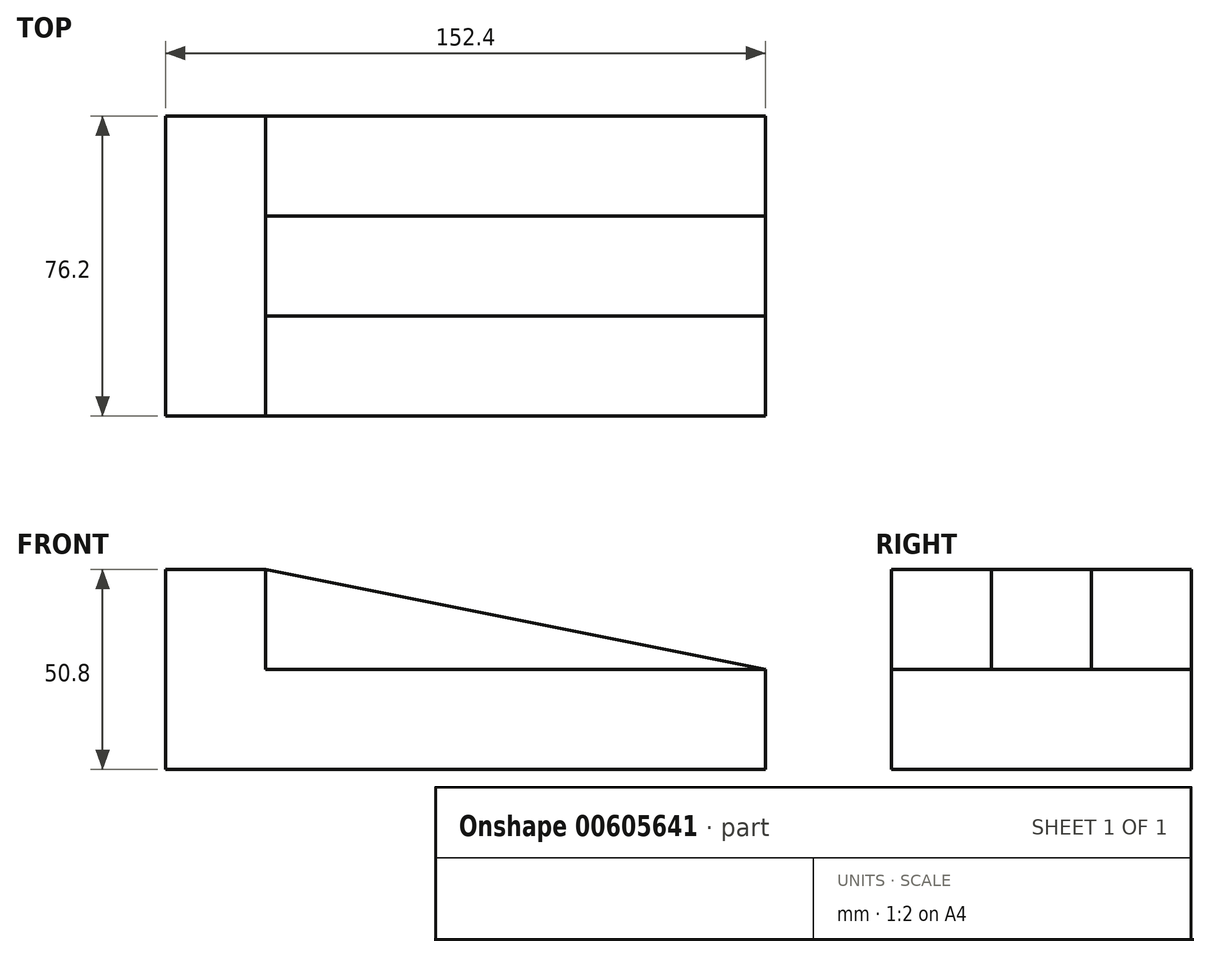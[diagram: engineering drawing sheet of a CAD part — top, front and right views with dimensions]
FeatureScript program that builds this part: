
annotation { "Feature Type Name" : "Feature", "Feature Type Description" : "" }
export const myFeature = defineFeature(function(context is Context, id is Id, definition is map)
    precondition{}
    {
        {
            var Q0;
            Q0=qCreatedBy(makeId("Front.planeOp"),FACE);
            var sketch = newSketch(context, id + "F0", { "sketchPlane" : qUnion([Q0])});
            skLineSegment(sketch, "E0", {"start": v(0, 0) * mm, "end": v(152.4, 0) * mm});
            skLineSegment(sketch, "E1", {"start": v(152.4, 0) * mm, "end": v(152.4, 50.8) * mm});
            skLineSegment(sketch, "E2", {"start": v(152.4, 50.8) * mm, "end": v(0, 50.8) * mm});
            skLineSegment(sketch, "E3", {"start": v(0, 50.8) * mm, "end": v(0, 0) * mm});
            skSolve(sketch);
        }
        {
            var Q0;
            Q0 = qSketchRegion(id + "F0", true);
            extrude(context, id + "F1", {"entities" : qUnion([Q0]), "depth" : 76.2 * mm, "offsetDistance" : 25.4 * mm});
        }
        {
            var Q0;
            Q0=makeQuery(id+"F1.opExtrude","CAP_FACE",FACE,{"disambiguationData":[OSD([sQuery(id+"F0.wireOp",EDGE,"E0"),sQuery(id+"F0.wireOp",EDGE,"E1"),sQuery(id+"F0.wireOp",EDGE,"E2"),sQuery(id+"F0.wireOp",EDGE,"E3")])],"isStart":false});
            var sketch = newSketch(context, id + "F2", { "sketchPlane" : qUnion([Q0])});
            skLineSegment(sketch, "E4", {"start": v(0, 50.8) * mm, "end": v(25.4, 50.8) * mm});
            skLineSegment(sketch, "E5", {"start": v(25.4, 50.8) * mm, "end": v(25.4, 25.4) * mm});
            skLineSegment(sketch, "E6", {"start": v(25.4, 25.4) * mm, "end": v(152.4, 25.4) * mm});
            skLineSegment(sketch, "E7", {"start": v(0, 50.8) * mm, "end": v(0, 0) * mm});
            skLineSegment(sketch, "E8", {"start": v(0, 0) * mm, "end": v(152.4, 0) * mm});
            skLineSegment(sketch, "E9", {"start": v(152.4, 0) * mm, "end": v(152.4, 25.4) * mm});
            skLineSegment(sketch, "E10", {"start": v(152.4, 25.4) * mm, "end": v(152.4, 0) * mm});
            skLineSegment(sketch, "E11", {"start": v(152.4, 0) * mm, "end": v(0, 0) * mm});
            skLineSegment(sketch, "E12", {"start": v(25.4, 50.8) * mm, "end": v(152.4, 50.8) * mm});
            skLineSegment(sketch, "E13", {"start": v(152.4, 50.8) * mm, "end": v(152.4, 25.4) * mm});
            skLineSegment(sketch, "E14", {"start": v(152.4, 25.4) * mm, "end": v(25.4, 25.4) * mm});
            skSolve(sketch);
        }
        {
            var Q0;
            Q0=makeQuery(id+"F2.imprint","IMPRINT",FACE,{"disambiguationData":[TD([[makeQuery(id+"F2.imprint","IMPRINT",EDGE,{"derivedFrom":sQuery(id+"F2.wireOp",EDGE,"E5")}),1.0]])]});
            extrude(context, id + "F3", {"entities" : qUnion([Q0]), "operationType" : NewBodyOperationType.REMOVE, "oppositeDirection" : true, "depth" : 25.4 * mm, "offsetDistance" : 25.4 * mm});
        }
        {
            var Q0;
            Q0=makeQuery(id+"F1.opExtrude","CAP_FACE",FACE,{"disambiguationData":[OSD([sQuery(id+"F0.wireOp",EDGE,"E0"),sQuery(id+"F0.wireOp",EDGE,"E1"),sQuery(id+"F0.wireOp",EDGE,"E2"),sQuery(id+"F0.wireOp",EDGE,"E3")])],"isStart":true});
            var sketch = newSketch(context, id + "F4", { "sketchPlane" : qUnion([Q0])});
            skLineSegment(sketch, "E15", {"start": v(0, 50.8) * mm, "end": v(-25.4, 50.8) * mm});
            skLineSegment(sketch, "E16", {"start": v(-25.4, 50.8) * mm, "end": v(-25.4, 25.4) * mm});
            skPoint(sketch, "E16.endSnap0", {"position": v(0, 25.4) * mm});
            skLineSegment(sketch, "E17", {"start": v(-25.4, 25.4) * mm, "end": v(-152.4, 25.4) * mm});
            skLineSegment(sketch, "E18", {"start": v(-152.4, 25.4) * mm, "end": v(-152.4, 0) * mm});
            skLineSegment(sketch, "E19", {"start": v(-152.4, 0) * mm, "end": v(0, 0) * mm});
            skLineSegment(sketch, "E20", {"start": v(0, 0) * mm, "end": v(0, 50.8) * mm});
            skLineSegment(sketch, "E21", {"start": v(-25.4, 50.8) * mm, "end": v(-152.4, 50.8) * mm});
            skLineSegment(sketch, "E22", {"start": v(-152.4, 50.8) * mm, "end": v(-152.4, 25.4) * mm});
            skLineSegment(sketch, "E23", {"start": v(-152.4, 25.4) * mm, "end": v(-25.4, 25.4) * mm});
            skSolve(sketch);
        }
        {
            var Q0;
            Q0=makeQuery(id+"F4.imprint","IMPRINT",FACE,{"disambiguationData":[TD([[makeQuery(id+"F4.imprint","IMPRINT",EDGE,{"derivedFrom":sQuery(id+"F4.wireOp",EDGE,"E16")}),-1.0]])]});
            extrude(context, id + "F5", {"entities" : qUnion([Q0]), "operationType" : NewBodyOperationType.REMOVE, "oppositeDirection" : true, "depth" : 25.4 * mm, "offsetDistance" : 25.4 * mm});
        }
        {
            var Q0;
            Q0=makeQuery(id+"F3.boolean.opBoolean","COPY",FACE,{"derivedFrom":makeQuery(id+"F3.opExtrude","CAP_FACE",FACE,{"disambiguationData":[OSD([sQuery(id+"F2.wireOp",EDGE,"E5"),sQuery(id+"F2.wireOp",EDGE,"E12"),sQuery(id+"F2.wireOp",EDGE,"E13"),sQuery(id+"F2.wireOp",EDGE,"E14")])],"isStart":false})});
            var sketch = newSketch(context, id + "F6", { "sketchPlane" : qUnion([Q0])});
            skLineSegment(sketch, "E24", {"start": v(25.4, 50.8) * mm, "end": v(152.4, 25.4) * mm});
            skLineSegment(sketch, "E25", {"start": v(152.4, 25.4) * mm, "end": v(152.4, 50.8) * mm});
            skLineSegment(sketch, "E26", {"start": v(152.4, 50.8) * mm, "end": v(25.4, 50.8) * mm});
            skSolve(sketch);
        }
        {
            var Q0;
            Q0=makeQuery(id+"F6.imprint","IMPRINT",FACE,{"disambiguationData":[TD([[makeQuery(id+"F6.imprint","IMPRINT",EDGE,{"derivedFrom":sQuery(id+"F6.wireOp",EDGE,"E24")}),1.0]])]});
            extrude(context, id + "F7", {"entities" : qUnion([Q0]), "operationType" : NewBodyOperationType.REMOVE, "oppositeDirection" : true, "depth" : 25.4 * mm, "offsetDistance" : 25.4 * mm});
        }
    });
